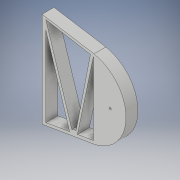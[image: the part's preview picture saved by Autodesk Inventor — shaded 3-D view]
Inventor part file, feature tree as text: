
AUTODESK INVENTOR PART (.ipt)
format: ipt  version: 2017 (Build 210142000, 142)  size: 131,584 bytes
history: native  units: mm
features: extrude x1, sketch x1
ambient origin geometry x8: Origin, YZ Plane, XZ Plane, XY Plane, X Axis, Y Axis, Z Axis, Center Point
bodies: Volumenkörper1 (feature_tree)
feature tree (2):
  extrude  "Extrusion1"  Depth=80.0mm
  sketch  "Skizze1"  dims[d6=150.0mm d8=80.0mm d9=17.453293mm d10=17.453293mm d12=60.5mm d15=62.0mm d16=3.4mm d17=40.0mm d18=15.0mm d22=5.0mm d23=5.0mm d25=5.0mm d26=5.0mm d27=3.147269mm d28=7.331654mm d29=160.0mm d30=80.0mm d31=67.0mm d32=20.0mm d33=0.0mm]
